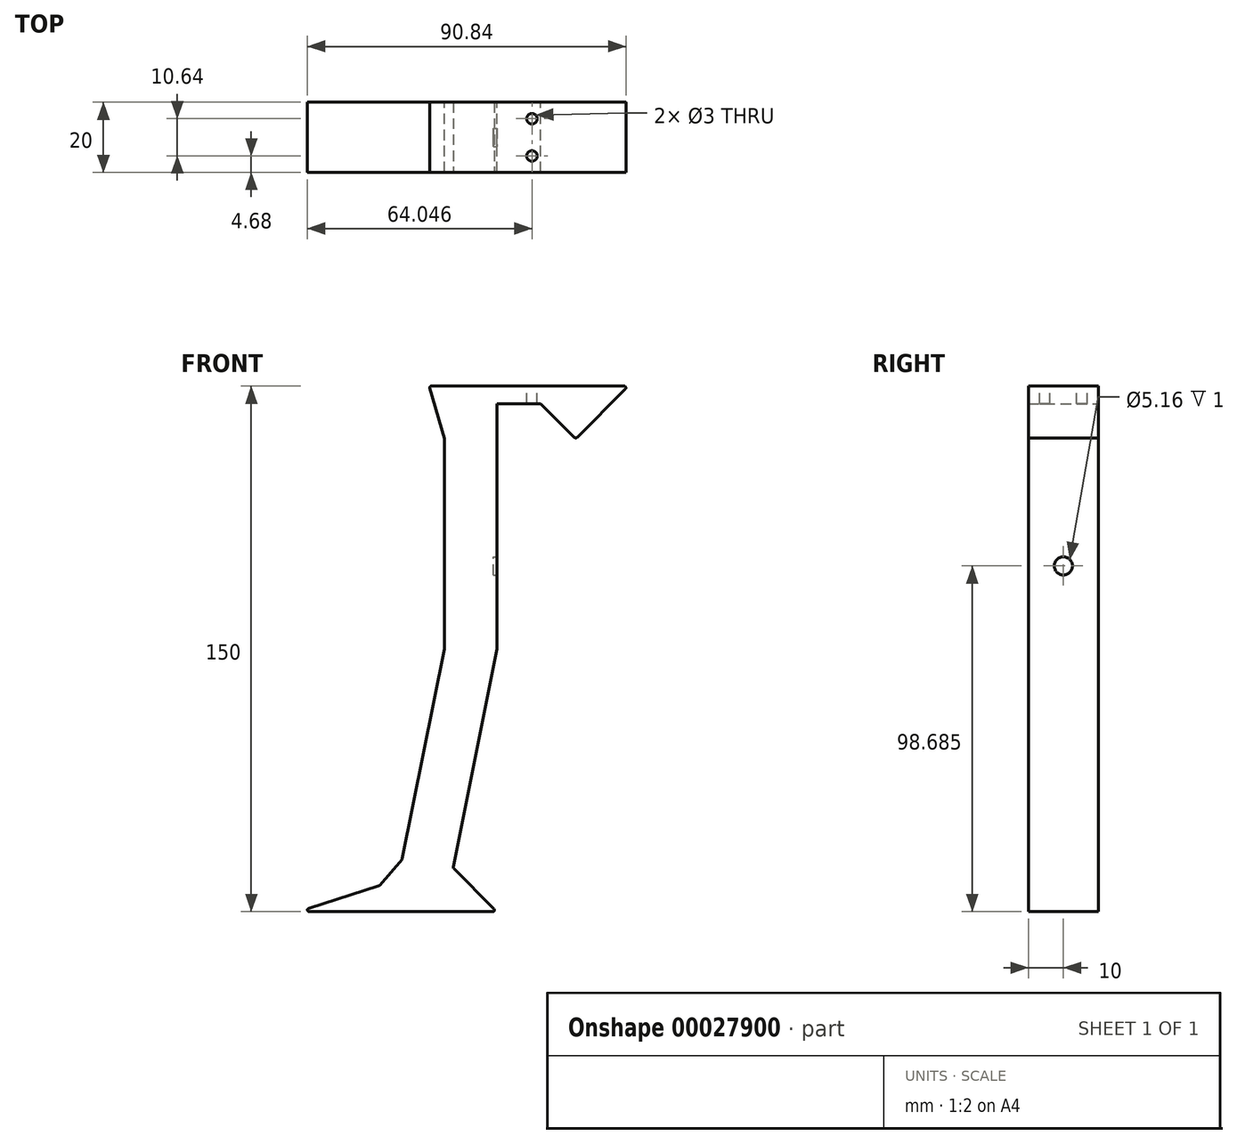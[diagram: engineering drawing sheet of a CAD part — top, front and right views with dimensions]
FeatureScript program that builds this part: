
annotation { "Feature Type Name" : "Feature", "Feature Type Description" : "" }
export const myFeature = defineFeature(function(context is Context, id is Id, definition is map)
    precondition{}
    {
        {
            var Q0;
            Q0=qCreatedBy(makeId("Front.planeOp"),FACE);
            var sketch = newSketch(context, id + "F0", { "sketchPlane" : qUnion([Q0])});
            skLineSegment(sketch, "E0.bottom", {"start": v(-46.95, 75) * mm, "end": v(28.05, 75) * mm});
            skLineSegment(sketch, "E0.top", {"start": v(-46.95, 0) * mm, "end": v(28.05, 0) * mm});
            skLineSegment(sketch, "E0.left", {"start": v(-46.95, 75) * mm, "end": v(-46.95, 0) * mm});
            skLineSegment(sketch, "E0.right", {"start": v(28.05, 75) * mm, "end": v(28.05, 0) * mm});
            skLineSegment(sketch, "E1", {"start": v(28.05, 60) * mm, "end": v(-31.95, 60) * mm});
            skLineSegment(sketch, "E2", {"start": v(-31.95, 60) * mm, "end": v(-31.95, 0) * mm});
            skLineSegment(sketch, "E3", {"start": v(-9.45, 75) * mm, "end": v(-9.45, 60) * mm});
            skLineSegment(sketch, "E4", {"start": v(-9.45, 60) * mm, "end": v(5.55, 75) * mm});
            skLineSegment(sketch, "E5", {"start": v(-46.95, 75) * mm, "end": v(-51.34, 75) * mm});
            skLineSegment(sketch, "E6", {"start": v(-51.34, 75) * mm, "end": v(-46.95, 60) * mm});
            skLineSegment(sketch, "E7", {"start": v(28.05, 0) * mm, "end": v(-46.95, -75) * mm});
            skLineSegment(sketch, "E8", {"start": v(-46.95, -75) * mm, "end": v(-61.95, -75) * mm});
            skLineSegment(sketch, "E9", {"start": v(-61.95, -75) * mm, "end": v(-46.95, 0) * mm});
            skLineSegment(sketch, "E10", {"start": v(-46.95, -75) * mm, "end": v(-31.95, 0) * mm});
            skLineSegment(sketch, "E11", {"start": v(-61.95, -75) * mm, "end": v(-71.95, -75) * mm});
            skLineSegment(sketch, "E12", {"start": v(-71.95, -75) * mm, "end": v(-58.95, -60) * mm});
            skLineSegment(sketch, "E13", {"start": v(-56.95, -75) * mm, "end": v(-43.95, -60) * mm});
            skLineSegment(sketch, "E14", {"start": v(-31.95, 19.68) * mm, "end": v(-31.95, 24.68) * mm});
            skLineSegment(sketch, "E15", {"start": v(-31.95, 60) * mm, "end": v(-31.95, 70) * mm});
            skLineSegment(sketch, "E16", {"start": v(-31.95, 70) * mm, "end": v(-9.45, 70) * mm});
            skPoint(sketch, "E16.endSnap0", {"position": v(-9.45, 67.5) * mm});
            skLineSegment(sketch, "E17", {"start": v(-19.45, 70) * mm, "end": v(-9.45, 60) * mm});
            skLineSegment(sketch, "E18", {"start": v(-65.45, -67.5) * mm, "end": v(-88.68, -75) * mm});
            skLineSegment(sketch, "E19", {"start": v(-88.68, -75) * mm, "end": v(-71.95, -75) * mm});
            skLineSegment(sketch, "E20", {"start": v(-46.95, -75) * mm, "end": v(-31.95, -75) * mm});
            skLineSegment(sketch, "E21", {"start": v(-31.95, -75) * mm, "end": v(-39.45, -67.5) * mm});
            skLineSegment(sketch, "E22", {"start": v(-39.45, -67.5) * mm, "end": v(-44.45, -62.5) * mm});
            skSolve(sketch);
        }
        {
            var Q0;
            {var subQ1=sQuery(id+"F0.wireOp",EDGE,"cec4a44a-0353-401e-a1ed-aaa4011a612b");Q0=makeQuery(id+"F0.imprint","IMPRINT",FACE,{"disambiguationData":[TD([[makeQuery(id+"F0.imprint","IMPRINT",EDGE,{"derivedFrom":subQ1}),1.0]])]});}
            var Q1;
            {var subQ3=sQuery(id+"F0.wireOp",EDGE,"E0.left");Q1=makeQuery(id+"F0.imprint","IMPRINT",FACE,{"disambiguationData":[TD([[makeQuery(id+"F0.imprint","IMPRINT",EDGE,{"derivedFrom":subQ3}),1.0]])]});}
            var Q2;
            {var subQ1=sQuery(id+"F0.wireOp",EDGE,"E3");Q2=makeQuery(id+"F0.imprint","IMPRINT",FACE,{"disambiguationData":[TD([[makeQuery(id+"F0.imprint","IMPRINT",EDGE,{"derivedFrom":subQ1}),1.0]])]});}
            var Q3;
            {var subQ1=sQuery(id+"F0.wireOp",EDGE,"E5");Q3=makeQuery(id+"F0.imprint","IMPRINT",FACE,{"disambiguationData":[TD([[makeQuery(id+"F0.imprint","IMPRINT",EDGE,{"derivedFrom":subQ1}),1.0]])]});}
            var Q4;
            {var subQ1=sQuery(id+"F0.wireOp",EDGE,"E13");Q4=makeQuery(id+"F0.imprint","IMPRINT",FACE,{"disambiguationData":[TD([[makeQuery(id+"F0.imprint","IMPRINT",EDGE,{"derivedFrom":subQ1}),1.0]])]});}
            var Q5;
            {var subQ1=sQuery(id+"F0.wireOp",EDGE,"E11");Q5=makeQuery(id+"F0.imprint","IMPRINT",FACE,{"disambiguationData":[TD([[makeQuery(id+"F0.imprint","IMPRINT",EDGE,{"derivedFrom":subQ1}),-1.0]])]});}
            var Q6;
            {var subQ0=sQuery(id+"F0.wireOp",EDGE,"E17");Q6=makeQuery(id+"F0.imprint","IMPRINT",FACE,{"disambiguationData":[TD([[makeQuery(id+"F0.imprint","IMPRINT",EDGE,{"derivedFrom":subQ0}),1.0]])]});}
            var Q7;
            {var subQ0=sQuery(id+"F0.wireOp",EDGE,"0af0b818-f1c4-4242-8e4c-e54c71e078cd");Q7=makeQuery(id+"F0.imprint","IMPRINT",FACE,{"disambiguationData":[TD([[makeQuery(id+"F0.imprint","IMPRINT",EDGE,{"derivedFrom":subQ0}),-1.0]])]});}
            var Q8;
            {var subQ0=sQuery(id+"F0.wireOp",EDGE,"E13");Q8=makeQuery(id+"F0.imprint","IMPRINT",FACE,{"disambiguationData":[TD([[makeQuery(id+"F0.imprint","IMPRINT",EDGE,{"derivedFrom":subQ0}),-1.0]])]});}
            var Q9;
            {var subQ0=sQuery(id+"F0.wireOp",EDGE,"E22");Q9=makeQuery(id+"F0.imprint","IMPRINT",FACE,{"disambiguationData":[TD([[makeQuery(id+"F0.imprint","IMPRINT",EDGE,{"derivedFrom":subQ0}),1.0]])]});}
            var Q10;
            {var subQ1=sQuery(id+"F0.wireOp",EDGE,"E20");Q10=makeQuery(id+"F0.imprint","IMPRINT",FACE,{"disambiguationData":[TD([[makeQuery(id+"F0.imprint","IMPRINT",EDGE,{"derivedFrom":subQ1}),1.0]])]});}
            var Q11;
            {var subQ1=sQuery(id+"F0.wireOp",EDGE,"E18");Q11=makeQuery(id+"F0.imprint","IMPRINT",FACE,{"disambiguationData":[TD([[makeQuery(id+"F0.imprint","IMPRINT",EDGE,{"derivedFrom":subQ1}),1.0]])]});}
            extrude(context, id + "F1", {"entities" : qUnion([Q0, Q1, Q2, Q3, Q4, Q5, Q6, Q7, Q8, Q9, Q10, Q11]), "depth" : 20 * mm});
        }
        {
            var Q0;
            Q0=makeQuery(id+"F1.opExtrude","SWEPT_FACE",FACE,{"disambiguationData":[OSD([sQuery(id+"F0.wireOp",EDGE,"E0.bottom")])]});
            var sketch = newSketch(context, id + "F2", { "sketchPlane" : qUnion([Q0])});
            skLineSegment(sketch, "E23", {"start": v(-51.34, -10) * mm, "end": v(5.55, -10) * mm, "construction": true});
            skCircle(sketch, "E24", {"center": v(-21.95, -15.32) * mm, "radius": 1.5 * mm});
            skCircle(sketch, "E25.MirrorC", {"center": v(-21.95, -4.68) * mm, "radius": 1.5 * mm});
            skSolve(sketch);
        }
        {
            var Q0;
            Q0=qSketchRegion(id+"F2",true);
            extrude(context, id + "F3", {"entities" : qUnion([Q0]), "operationType" : NewBodyOperationType.REMOVE, "oppositeDirection" : true, "depth" : 20 * mm});
        }
        {
            var Q0;
            Q0=makeQuery(id+"F1.opExtrude","SWEPT_FACE",FACE,{"disambiguationData":[OSD([sQuery(id+"F0.wireOp",EDGE,"E2"),sQuery(id+"F0.wireOp",EDGE,"E14")])]});
            var sketch = newSketch(context, id + "F4", { "sketchPlane" : qUnion([Q0])});
            skCircle(sketch, "E26", {"center": v(-10, 23.68) * mm, "radius": 2.58 * mm});
            skLineSegment(sketch, "E27", {"start": v(0, 32.7) * mm, "end": v(0, 17.66) * mm, "construction": true});
            skLineSegment(sketch, "E28", {"start": v(-20, 17.66) * mm, "end": v(-20, 32.7) * mm, "construction": true});
            skLineSegment(sketch, "E29", {"start": v(-20, 32.7) * mm, "end": v(-20, 17.66) * mm, "construction": true});
            skSolve(sketch);
        }
        {
            var Q0;
            Q0=qSketchRegion(id+"F4",true);
            extrude(context, id + "F5", {"entities" : qUnion([Q0]), "operationType" : NewBodyOperationType.REMOVE, "oppositeDirection" : true, "depth" : 1 * mm});
        }
        {
            var Q0;
            Q0=makeQuery(id+"F1.opExtrude","SWEPT_EDGE",EDGE,{"disambiguationData":[OSD([sQuery(id+"F0.wireOp",EDGE,"E0.bottom"),sQuery(id+"F0.wireOp",EDGE,"E4")])]});
            var Q1;
            Q1=makeQuery(id+"F1.opExtrude","SWEPT_EDGE",EDGE,{"disambiguationData":[OSD([sQuery(id+"F0.wireOp",EDGE,"E1"),sQuery(id+"F0.wireOp",EDGE,"E3"),sQuery(id+"F0.wireOp",EDGE,"E4"),sQuery(id+"F0.wireOp",EDGE,"E17")])]});
            var Q2;
            Q2=makeQuery(id+"F1.opExtrude","SWEPT_EDGE",EDGE,{"disambiguationData":[OSD([sQuery(id+"F0.wireOp",EDGE,"E5"),sQuery(id+"F0.wireOp",EDGE,"E6")])]});
            var Q3;
            Q3=makeQuery(id+"F1.opExtrude","SWEPT_EDGE",EDGE,{"disambiguationData":[OSD([sQuery(id+"F0.wireOp",EDGE,"E0.left"),sQuery(id+"F0.wireOp",EDGE,"E6")])]});
            var Q4;
            Q4=makeQuery(id+"F1.opExtrude","SWEPT_EDGE",EDGE,{"disambiguationData":[OSD([sQuery(id+"F0.wireOp",EDGE,"E0.top"),sQuery(id+"F0.wireOp",EDGE,"E2"),sQuery(id+"F0.wireOp",EDGE,"E10")])]});
            var Q5;
            Q5=makeQuery(id+"F1.opExtrude","SWEPT_EDGE",EDGE,{"disambiguationData":[OSD([sQuery(id+"F0.wireOp",EDGE,"E0.top"),sQuery(id+"F0.wireOp",EDGE,"E0.left"),sQuery(id+"F0.wireOp",EDGE,"E9")])]});
            var Q6;
            Q6=makeQuery(id+"F1.opExtrude","SWEPT_EDGE",EDGE,{"disambiguationData":[OSD([sQuery(id+"F0.wireOp",EDGE,"E10"),sQuery(id+"F0.wireOp",EDGE,"E22")])]});
            var Q7;
            Q7=makeQuery(id+"F1.opExtrude","SWEPT_EDGE",EDGE,{"disambiguationData":[OSD([sQuery(id+"F0.wireOp",EDGE,"E9"),sQuery(id+"F0.wireOp",EDGE,"E12")])]});
            var Q8;
            Q8=makeQuery(id+"F1.opExtrude","SWEPT_EDGE",EDGE,{"disambiguationData":[OSD([sQuery(id+"F0.wireOp",EDGE,"E12"),sQuery(id+"F0.wireOp",EDGE,"E18")])]});
            var Q9;
            Q9=makeQuery(id+"F1.opExtrude","SWEPT_EDGE",EDGE,{"disambiguationData":[OSD([sQuery(id+"F0.wireOp",EDGE,"E20"),sQuery(id+"F0.wireOp",EDGE,"E21")])]});
            var Q10;
            Q10=makeQuery(id+"F1.opExtrude","SWEPT_EDGE",EDGE,{"disambiguationData":[OSD([sQuery(id+"F0.wireOp",EDGE,"E18"),sQuery(id+"F0.wireOp",EDGE,"E19")])]});
            fillet(context, id + "F6", {"entities" : qUnion([Q0, Q1, Q2, Q3, Q4, Q5, Q6, Q7, Q8, Q9, Q10]), "radius" : .5 * mm, "tangentPropagation" : true, "allowEdgeOverflow" : false});
        }
    });
